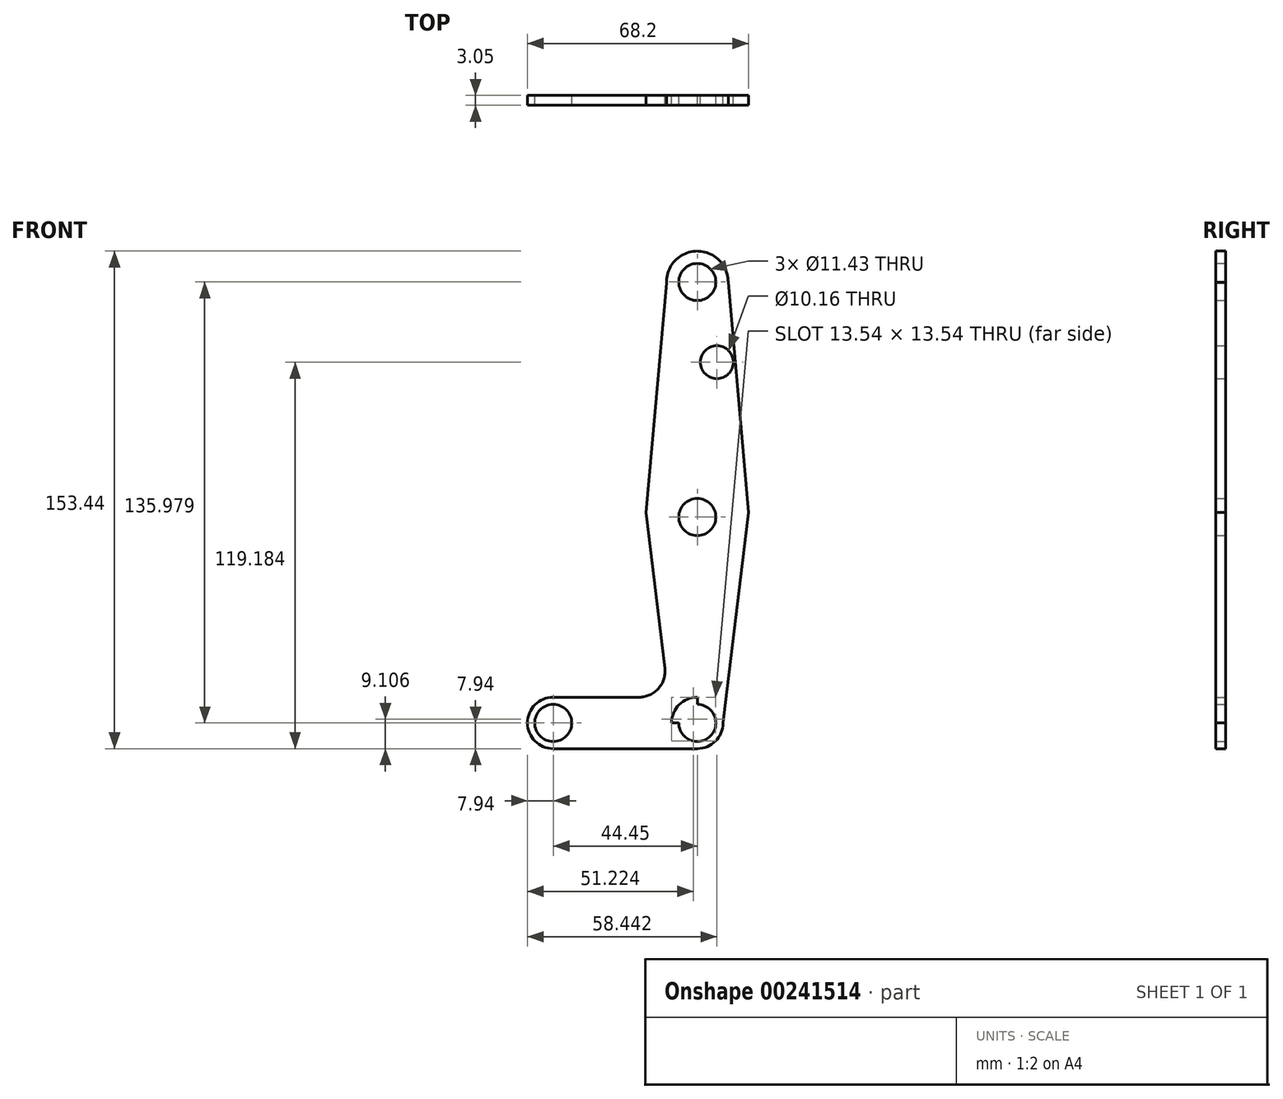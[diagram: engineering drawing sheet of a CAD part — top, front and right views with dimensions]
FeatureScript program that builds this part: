
annotation { "Feature Type Name" : "Feature", "Feature Type Description" : "" }
export const myFeature = defineFeature(function(context is Context, id is Id, definition is map)
    precondition{}
    {
        {
            var Q0;
            Q0=qCreatedBy(makeId("Front.planeOp"),FACE);
            var sketch = newSketch(context, id + "F0", { "sketchPlane" : qUnion([Q0])});
            skLineSegment(sketch, "E0", {"start": v(0, 63.5) * mm, "end": v(0, 135.98) * mm});
            skCircle(sketch, "E1", {"center": v(0, 135.98) * mm, "radius": 9.53 * mm});
            skCircle(sketch, "E2", {"center": v(0, 0) * mm, "radius": 7.94 * mm});
            skLineSegment(sketch, "E3", {"start": v(0, 0) * mm, "end": v(-44.45, 0) * mm});
            skCircle(sketch, "E4", {"center": v(-44.45, 0) * mm, "radius": 7.94 * mm});
            skLineSegment(sketch, "E5", {"start": v(9.52, 135.96) * mm, "end": v(15.81, 64.9) * mm});
            skLineSegment(sketch, "E6", {"start": v(-9.52, 135.7) * mm, "end": v(-15.81, 64.9) * mm});
            skLineSegment(sketch, "E7", {"start": v(-17.92, 7.94) * mm, "end": v(-44.45, 7.94) * mm});
            skLineSegment(sketch, "E8", {"start": v(0, -7.94) * mm, "end": v(-44.45, -7.94) * mm});
            skCircle(sketch, "E9", {"center": v(0, 135.98) * mm, "radius": 5.72 * mm});
            skLineSegment(sketch, "E10", {"start": v(0, 63.5) * mm, "end": v(0, 0) * mm});
            skCircle(sketch, "E11", {"center": v(6.05, 111.24) * mm, "radius": 5.08 * mm});
            skCircle(sketch, "E12", {"center": v(0, 63.5) * mm, "radius": 5.72 * mm});
            skCircle(sketch, "E13", {"center": v(0, 0) * mm, "radius": 5.71 * mm});
            skCircle(sketch, "E14", {"center": v(-44.45, 0) * mm, "radius": 5.72 * mm});
            skLineSegment(sketch, "E15", {"start": v(-15.81, 64.9) * mm, "end": v(-10.02, 16.84) * mm});
            skPoint(sketch, "E16.newPointB", {"position": v(-8, 0) * mm});
            skArc(sketch, "E16.filletArc", {"start": v(-17.92, 7.94) * mm, "mid": v(-11.97, 10.61) * mm, "end": v(-10.02, 16.84) * mm});
            skLineSegment(sketch, "E17", {"start": v(15.81, 64.9) * mm, "end": v(7.94, 0) * mm});
            skSolve(sketch);
        }
        {
            var Q0;
            Q0 = qSketchRegion(id + "F0", true);
            extrude(context, id + "F1", {"entities" : qUnion([Q0]), "depth" : 3.05 * mm});
        }
        {
            var Q0;
            {var subQ0=sQuery(id+"F0.wireOp",EDGE,"E11");var subQ1=sQuery(id+"F0.wireOp",EDGE,"E5");var subQ2=makeQuery(id+"F0.imprint","INTERSECT",VERTEX,{"disambiguationData":[OD(0.0)],"derivedFrom":[subQ1,subQ0]});Q0=makeQuery(id+"F0.imprint","IMPRINT",FACE,{"disambiguationData":[TD([[makeQuery(id+"F0.imprint","IMPRINT",EDGE,{"disambiguationData":[TD([[subQ2,-1.0]])],"derivedFrom":subQ1}),-1.0]])]});}
            var Q1;
            Q1=sQuery(id+"F0.wireOp",EDGE,"E11");
            extrude(context, id + "F2", {"entities" : qUnion([Q0]), "operationType" : NewBodyOperationType.ADD, "surfaceEntities" : qUnion([Q1]), "depth" : 3.05 * mm});
        }
    });
